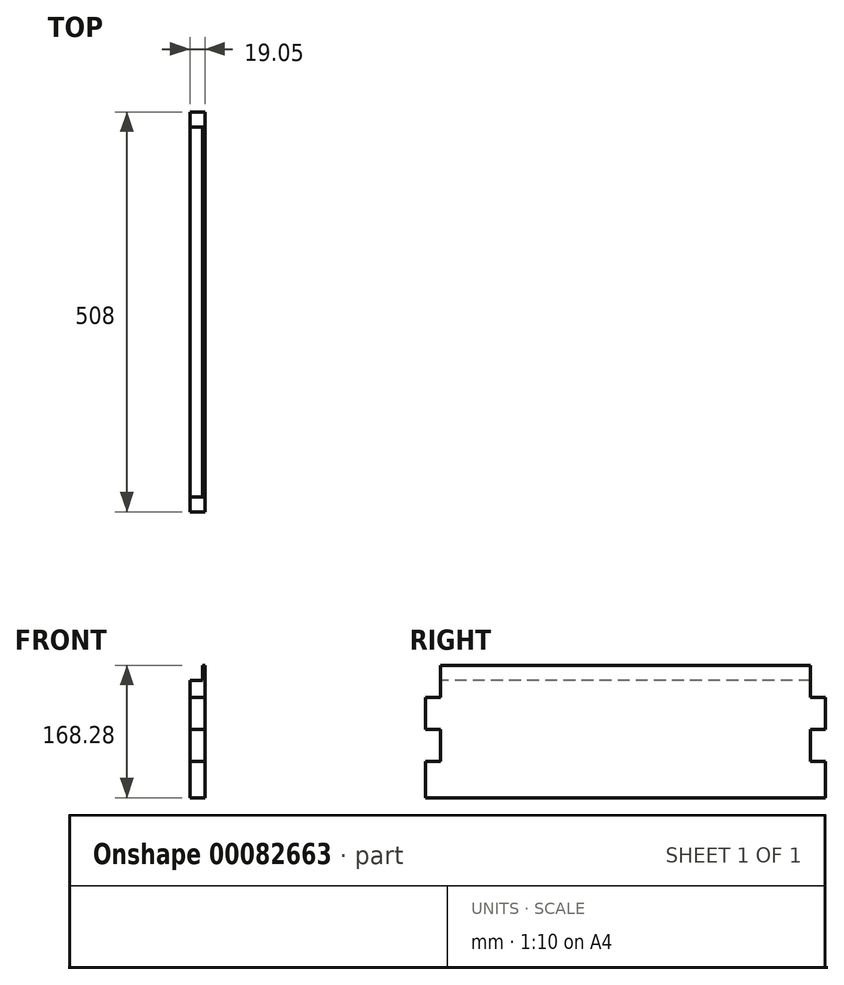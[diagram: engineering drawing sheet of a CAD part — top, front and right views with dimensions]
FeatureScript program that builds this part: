
annotation { "Feature Type Name" : "Feature", "Feature Type Description" : "" }
export const myFeature = defineFeature(function(context is Context, id is Id, definition is map)
    precondition{}
    {
        {
            var Q0;
            Q0=qCreatedBy(makeId("Right.planeOp"),FACE);
            var sketch = newSketch(context, id + "F0", { "sketchPlane" : qUnion([Q0])});
            skLineSegment(sketch, "E0.bottom", {"start": v(-257.36, 45.79) * mm, "end": v(250.64, 45.79) * mm});
            skLineSegment(sketch, "E0.top", {"start": v(-257.36, -122.49) * mm, "end": v(250.64, -122.49) * mm});
            skLineSegment(sketch, "E0.left", {"start": v(-257.36, 45.79) * mm, "end": v(-257.36, -122.49) * mm});
            skLineSegment(sketch, "E0.right", {"start": v(250.64, 45.79) * mm, "end": v(250.64, -122.49) * mm});
            skSolve(sketch);
        }
        {
            var Q0;
            Q0=makeQuery(id+"F0.imprint","IMPRINT",FACE,{"disambiguationData":[TD([[makeQuery(id+"F0.imprint","IMPRINT",EDGE,{"derivedFrom":sQuery(id+"F0.wireOp",EDGE,"E0.bottom")}),-1.0]])]});
            extrude(context, id + "F1", {"entities" : qUnion([Q0]), "depth" : 19.05 * mm});
        }
        {
            var Q0;
            Q0=makeQuery(id+"F1.opExtrude","CAP_FACE",FACE,{"disambiguationData":[OSD([sQuery(id+"F0.wireOp",EDGE,"E0.bottom"),sQuery(id+"F0.wireOp",EDGE,"E0.top"),sQuery(id+"F0.wireOp",EDGE,"E0.left"),sQuery(id+"F0.wireOp",EDGE,"E0.right")])],"isStart":false});
            var sketch = newSketch(context, id + "F2", { "sketchPlane" : qUnion([Q0])});
            skLineSegment(sketch, "E1.bottom", {"start": v(-257.36, 45.79) * mm, "end": v(-238.3, 45.79) * mm});
            skLineSegment(sketch, "E1.top", {"start": v(-257.36, 5.15) * mm, "end": v(-238.3, 5.15) * mm});
            skLineSegment(sketch, "E1.left", {"start": v(-257.36, 45.79) * mm, "end": v(-257.36, 5.15) * mm});
            skLineSegment(sketch, "E1.right", {"start": v(-238.3, 45.79) * mm, "end": v(-238.3, 5.15) * mm});
            skLineSegment(sketch, "E2.top", {"start": v(-257.36, -35.5) * mm, "end": v(-238.3, -35.5) * mm});
            skLineSegment(sketch, "E2.left", {"start": v(-257.36, 5.15) * mm, "end": v(-257.36, -35.5) * mm});
            skLineSegment(sketch, "E2.right", {"start": v(-238.3, 5.15) * mm, "end": v(-238.3, -35.5) * mm});
            skLineSegment(sketch, "E3.top", {"start": v(-257.36, -76.13) * mm, "end": v(-238.3, -76.13) * mm});
            skLineSegment(sketch, "E3.left", {"start": v(-257.36, -35.5) * mm, "end": v(-257.36, -76.13) * mm});
            skLineSegment(sketch, "E3.right", {"start": v(-238.3, -35.5) * mm, "end": v(-238.3, -76.13) * mm});
            skLineSegment(sketch, "E4.top", {"start": v(-257.36, -116.77) * mm, "end": v(-238.3, -116.77) * mm});
            skLineSegment(sketch, "E4.left", {"start": v(-257.36, -76.13) * mm, "end": v(-257.36, -116.77) * mm});
            skLineSegment(sketch, "E4.right", {"start": v(-238.3, -76.13) * mm, "end": v(-238.3, -116.77) * mm});
            skLineSegment(sketch, "E5.top", {"start": v(-257.36, -157.41) * mm, "end": v(-238.3, -157.41) * mm});
            skLineSegment(sketch, "E5.left", {"start": v(-257.36, -116.77) * mm, "end": v(-257.36, -157.41) * mm});
            skLineSegment(sketch, "E5.right", {"start": v(-238.3, -116.77) * mm, "end": v(-238.3, -157.41) * mm});
            skLineSegment(sketch, "E6.top", {"start": v(-257.36, -122.49) * mm, "end": v(-238.3, -122.49) * mm});
            skLineSegment(sketch, "E6.left", {"start": v(-257.36, -122.49) * mm, "end": v(-257.36, -157.41) * mm});
            skLineSegment(sketch, "E6.right", {"start": v(-238.3, -122.49) * mm, "end": v(-238.3, -157.41) * mm});
            skLineSegment(sketch, "E7", {"start": v(-3.36, 45.79) * mm, "end": v(-3.36, -122.49) * mm, "construction": true});
            skLineSegment(sketch, "E8.MirrorCS", {"start": v(250.64, -157.41) * mm, "end": v(231.6, -157.41) * mm});
            skLineSegment(sketch, "E9.MirrorCS", {"start": v(250.64, -35.5) * mm, "end": v(231.6, -35.5) * mm});
            skLineSegment(sketch, "E10.MirrorCS", {"start": v(250.64, 5.15) * mm, "end": v(231.6, 5.15) * mm});
            skLineSegment(sketch, "E11.MirrorCS", {"start": v(250.64, -76.13) * mm, "end": v(231.6, -76.13) * mm});
            skLineSegment(sketch, "E12.MirrorCS", {"start": v(250.64, -116.77) * mm, "end": v(231.6, -116.77) * mm});
            skLineSegment(sketch, "E13.MirrorCS", {"start": v(250.64, -122.49) * mm, "end": v(250.64, -157.41) * mm});
            skLineSegment(sketch, "E14.MirrorCS", {"start": v(250.64, 45.79) * mm, "end": v(250.64, 5.15) * mm});
            skLineSegment(sketch, "E15.MirrorCS", {"start": v(250.64, -122.49) * mm, "end": v(231.6, -122.49) * mm});
            skLineSegment(sketch, "E16.MirrorCS", {"start": v(250.64, -76.13) * mm, "end": v(250.64, -116.77) * mm});
            skLineSegment(sketch, "E17.MirrorCS", {"start": v(250.64, 45.79) * mm, "end": v(231.6, 45.79) * mm});
            skLineSegment(sketch, "E18.MirrorCS", {"start": v(250.64, -35.5) * mm, "end": v(250.64, -76.13) * mm});
            skLineSegment(sketch, "E19.MirrorCS", {"start": v(231.6, 5.15) * mm, "end": v(231.6, -35.5) * mm});
            skLineSegment(sketch, "E20.MirrorCS", {"start": v(250.64, 5.15) * mm, "end": v(250.64, -35.5) * mm});
            skLineSegment(sketch, "E21.MirrorCS", {"start": v(231.6, -116.77) * mm, "end": v(231.6, -157.41) * mm});
            skLineSegment(sketch, "E22.MirrorCS", {"start": v(231.6, -76.13) * mm, "end": v(231.6, -116.77) * mm});
            skLineSegment(sketch, "E23.MirrorCS", {"start": v(231.6, -35.5) * mm, "end": v(231.6, -76.13) * mm});
            skLineSegment(sketch, "E24.MirrorCS", {"start": v(231.6, -122.49) * mm, "end": v(231.6, -157.41) * mm});
            skLineSegment(sketch, "E25.MirrorCS", {"start": v(250.64, -116.77) * mm, "end": v(250.64, -157.41) * mm});
            skLineSegment(sketch, "E26.MirrorCS", {"start": v(231.6, 45.79) * mm, "end": v(231.6, 5.15) * mm});
            skSolve(sketch);
        }
        {
            var Q0;
            Q0=makeQuery(id+"F2.imprint","IMPRINT",FACE,{"disambiguationData":[TD([[makeQuery(id+"F2.imprint","IMPRINT",EDGE,{"derivedFrom":sQuery(id+"F2.wireOp",EDGE,"E14.MirrorCS")}),-1.0]])]});
            var Q1;
            Q1=makeQuery(id+"F2.imprint","IMPRINT",FACE,{"disambiguationData":[TD([[makeQuery(id+"F2.imprint","IMPRINT",EDGE,{"derivedFrom":sQuery(id+"F2.wireOp",EDGE,"E18.MirrorCS")}),-1.0]])]});
            var Q2;
            Q2=makeQuery(id+"F2.imprint","IMPRINT",FACE,{"disambiguationData":[TD([[makeQuery(id+"F2.imprint","IMPRINT",EDGE,{"derivedFrom":sQuery(id+"F2.wireOp",EDGE,"E8.MirrorCS")}),-1.0]])]});
            var Q3;
            Q3=makeQuery(id+"F2.imprint","IMPRINT",FACE,{"disambiguationData":[TD([[makeQuery(id+"F2.imprint","IMPRINT",EDGE,{"derivedFrom":sQuery(id+"F2.wireOp",EDGE,"E2.top")}),-1.0]])]});
            var Q4;
            Q4=makeQuery(id+"F2.imprint","IMPRINT",FACE,{"disambiguationData":[TD([[makeQuery(id+"F2.imprint","IMPRINT",EDGE,{"derivedFrom":sQuery(id+"F2.wireOp",EDGE,"E1.bottom")}),-1.0]])]});
            extrude(context, id + "F3", {"entities" : qUnion([Q0, Q1, Q2, Q3, Q4]), "operationType" : NewBodyOperationType.REMOVE, "oppositeDirection" : true, "depth" : 25.4 * mm});
        }
        {
            var Q0;
            Q0=makeQuery(id+"F1.opExtrude","CAP_FACE",FACE,{"disambiguationData":[OSD([sQuery(id+"F0.wireOp",EDGE,"E0.bottom"),sQuery(id+"F0.wireOp",EDGE,"E0.top"),sQuery(id+"F0.wireOp",EDGE,"E0.left"),sQuery(id+"F0.wireOp",EDGE,"E0.right")])],"isStart":true});
            var sketch = newSketch(context, id + "F4", { "sketchPlane" : qUnion([Q0])});
            skLineSegment(sketch, "E27", {"start": v(-231.6, 45.79) * mm, "end": v(-231.6, 26.74) * mm, "construction": true});
            skLineSegment(sketch, "E28", {"start": v(-231.6, 26.74) * mm, "end": v(238.3, 26.74) * mm});
            skLineSegment(sketch, "E29", {"start": v(238.3, 26.74) * mm, "end": v(238.3, 45.79) * mm});
            skLineSegment(sketch, "E30", {"start": v(238.3, 45.79) * mm, "end": v(-231.6, 45.79) * mm});
            skSolve(sketch);
        }
        {
            var Q0;
            Q0=qSketchRegion(id+"F4",true);
            var Q1;
            {var subQ0=sQuery(id+"F4.wireOp",EDGE,"E28");Q1=makeQuery(id+"F4.imprint","IMPRINT",FACE,{"disambiguationData":[TD([[makeQuery(id+"F4.imprint","IMPRINT",EDGE,{"derivedFrom":subQ0}),1.0]])]});}
            extrude(context, id + "F5", {"entities" : qUnion([Q0, Q1]), "operationType" : NewBodyOperationType.REMOVE, "oppositeDirection" : true, "depth" : 15.88 * mm});
        }
    });
